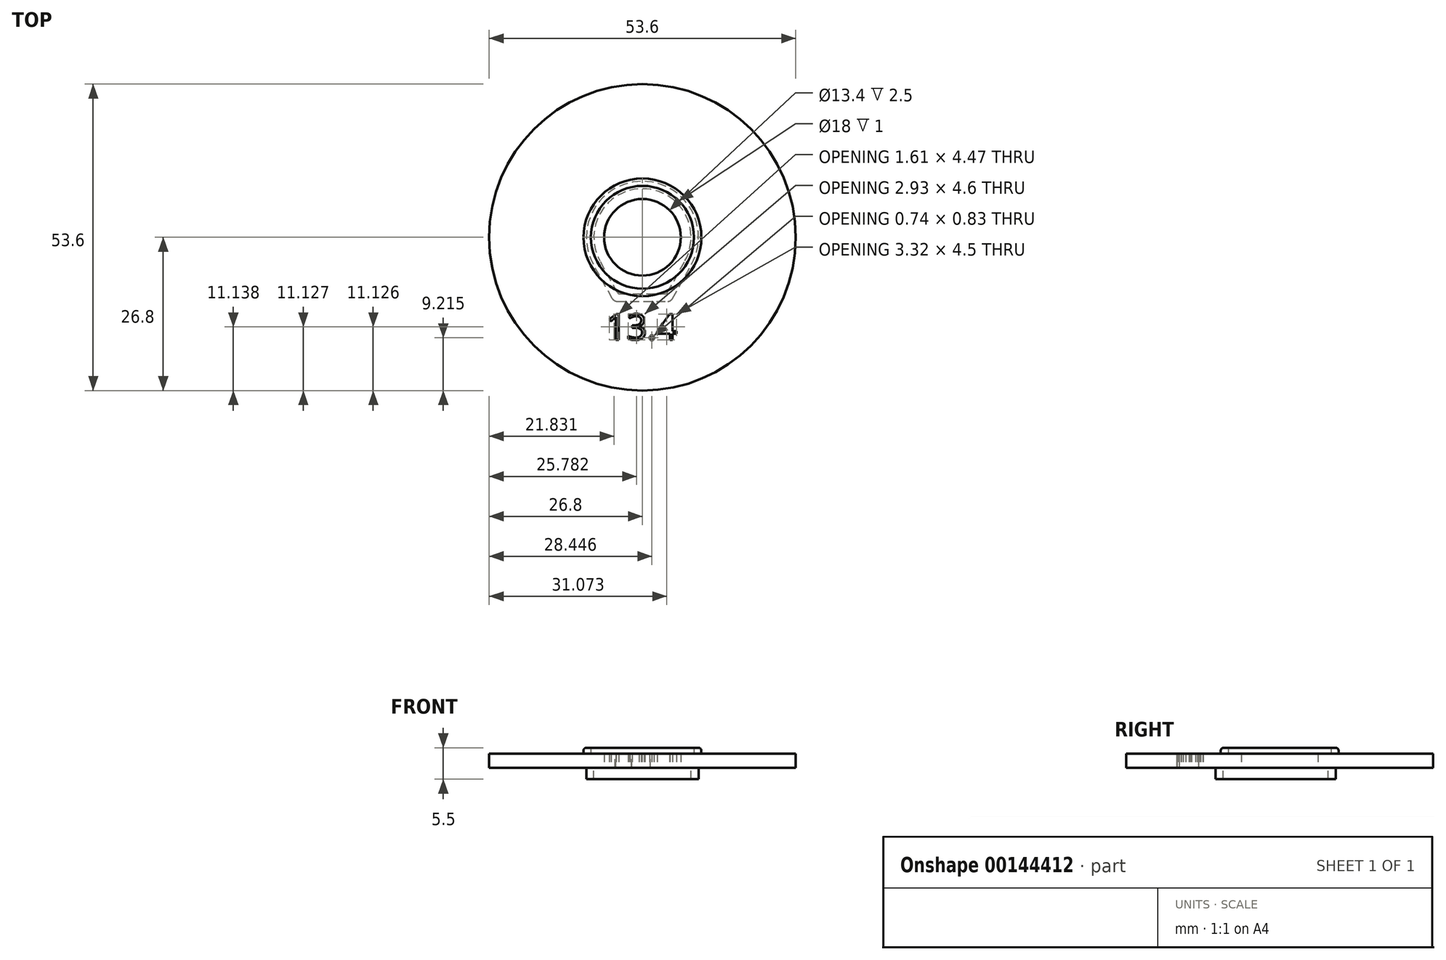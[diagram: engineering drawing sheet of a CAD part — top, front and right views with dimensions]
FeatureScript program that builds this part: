
annotation { "Feature Type Name" : "Feature", "Feature Type Description" : "" }
export const myFeature = defineFeature(function(context is Context, id is Id, definition is map)
    precondition{}
    {
        {
            assignVariable(context, id + "F0", {"name" : "shell_thickness", "anyValue" : 2.5 * mm});
        }
        {
            assignVariable(context, id + "F1", {"name" : "upper_ridge_height", "anyValue" : 1 * mm});
        }
        {
            assignVariable(context, id + "F2", {"name" : "lower_ridge_height", "anyValue" : 2 * mm});
        }
        {
            var Q0;
            Q0=qCreatedBy(makeId("Top.planeOp"),FACE);
            var sketch = newSketch(context, id + "F3", { "sketchPlane" : qUnion([Q0])});
            skCircle(sketch, "E0", {"center": v(0, 0) * mm, "radius": 26.8 * mm});
            skCircle(sketch, "E1", {"center": v(0, 0) * mm, "radius": 6.7 * mm});
            skLineSegment(sketch, "E2", {"start": v(0, 0) * mm, "end": v(0, -26.8) * mm, "construction": true});
            skText(sketch, "E3", { "text": "13.4", "fontName": "OpenSans-Regular.ttf"});
            const initialGuessF3  = {"E3": [-0.00635, -0.01791, 1, 0, 0.00451]};
            skSetInitialGuess(sketch, initialGuessF3);
            skSolve(sketch);
        }
        {
            var Q0;
            Q0=makeQuery(id+"F3.imprint","IMPRINT",FACE,{"disambiguationData":[TD([[makeQuery(id+"F3.imprint","IMPRINT",EDGE,{"derivedFrom":sQuery(id+"F3.wireOp",EDGE,"E0")}),1.0]])]});
            extrude(context, id + "F4", {"entities" : qUnion([Q0]), "depth" : getVariable(context, 'shell_thickness')});
        }
        {
            var Q0;
            Q0=makeQuery(id+"F4.opExtrude","CAP_FACE",FACE,{"disambiguationData":[OSD([sQuery(id+"F3.wireOp",EDGE,"E0"),sQuery(id+"F3.wireOp",EDGE,"E1")])],"isStart":false});
            var sketch = newSketch(context, id + "F5", { "sketchPlane" : qUnion([Q0])});
            skCircle(sketch, "E4.0", {"center": v(0, 0) * mm, "radius": 6.7 * mm});
            skCircle(sketch, "E5", {"center": v(0, 0) * mm, "radius": 9 * mm});
            skCircle(sketch, "E6", {"center": v(0, 0) * mm, "radius": 10.3 * mm});
            skSolve(sketch);
        }
        {
            var Q0;
            Q0=makeQuery(id+"F5.imprint","IMPRINT",FACE,{"disambiguationData":[TD([[makeQuery(id+"F5.imprint","IMPRINT",EDGE,{"derivedFrom":sQuery(id+"F5.wireOp",EDGE,"E5")}),-1.0]])]});
            extrude(context, id + "F6", {"entities" : qUnion([Q0]), "operationType" : NewBodyOperationType.ADD, "depth" : getVariable(context, 'upper_ridge_height')});
        }
        {
            var Q0;
            Q0=makeQuery(id+"F6.opExtrude","CAP_EDGE",EDGE,{"disambiguationData":[OSD([sQuery(id+"F5.wireOp",EDGE,"E6")])],"isStart":false});
            fillet(context, id + "F7", {"entities" : qUnion([Q0]), "radius" : 0.5 * mm, "tangentPropagation" : true, "allowEdgeOverflow" : false});
        }
        {
            var Q0;
            Q0=makeQuery(id+"F4.opExtrude","CAP_FACE",FACE,{"disambiguationData":[OSD([sQuery(id+"F3.wireOp",EDGE,"E0"),sQuery(id+"F3.wireOp",EDGE,"E1")])],"isStart":true});
            var sketch = newSketch(context, id + "F8", { "sketchPlane" : qUnion([Q0])});
            skPoint(sketch, "E7.0", {"position": v(0, 0) * mm});
            skCircle(sketch, "E8.0", {"center": v(0, 0) * mm, "radius": 6.7 * mm});
            skArc(sketch, "E9", {"start": v(-7.44, 4.12) * mm, "mid": v(0, -8.5) * mm, "end": v(7.44, 4.12) * mm});
            skArc(sketch, "E10.0", {"start": v(-8.57, 4.75) * mm, "mid": v(0, -9.8) * mm, "end": v(8.57, 4.75) * mm});
            skLineSegment(sketch, "E11", {"start": v(-4.41, 11.2) * mm, "end": v(4.41, 11.2) * mm});
            skLineSegment(sketch, "E12.0", {"start": v(-3.94, 9.9) * mm, "end": v(3.94, 9.9) * mm});
            skLineSegment(sketch, "E13", {"start": v(-5.29, 10.68) * mm, "end": v(-8.57, 4.75) * mm});
            skLineSegment(sketch, "E14", {"start": v(5.29, 10.68) * mm, "end": v(8.57, 4.75) * mm});
            skLineSegment(sketch, "E15.0", {"start": v(-4.38, 9.64) * mm, "end": v(-7.44, 4.12) * mm});
            skLineSegment(sketch, "E16.0", {"start": v(4.38, 9.64) * mm, "end": v(7.44, 4.12) * mm});
            skPoint(sketch, "E17.visualSharp", {"position": v(-5, 11.2) * mm});
            skArc(sketch, "E17.filletArc", {"start": v(-4.41, 11.2) * mm, "mid": v(-4.92, 11.06) * mm, "end": v(-5.29, 10.68) * mm});
            skPoint(sketch, "E18.visualSharp", {"position": v(5, 11.2) * mm});
            skArc(sketch, "E18.filletArc", {"start": v(5.29, 10.68) * mm, "mid": v(4.92, 11.06) * mm, "end": v(4.41, 11.2) * mm});
            skPoint(sketch, "E19.visualSharp", {"position": v(-4.23, 9.9) * mm});
            skArc(sketch, "E19.filletArc", {"start": v(-3.94, 9.9) * mm, "mid": v(-4.2, 9.83) * mm, "end": v(-4.38, 9.64) * mm});
            skPoint(sketch, "E20.visualSharp", {"position": v(4.23, 9.9) * mm});
            skArc(sketch, "E20.filletArc", {"start": v(4.38, 9.64) * mm, "mid": v(4.2, 9.83) * mm, "end": v(3.94, 9.9) * mm});
            skSolve(sketch);
        }
        {
            var Q0;
            Q0=makeQuery(id+"F8.imprint","IMPRINT",FACE,{"disambiguationData":[TD([[makeQuery(id+"F8.imprint","IMPRINT",EDGE,{"derivedFrom":sQuery(id+"F8.wireOp",EDGE,"E9")}),-1.0]])]});
            extrude(context, id + "F9", {"entities" : qUnion([Q0]), "operationType" : NewBodyOperationType.ADD, "depth" : getVariable(context, 'lower_ridge_height')});
        }
    });
